# Revit family: okamura_81K2LH00-81K20KH_Zart_Swivel models With arm
name_source: partatom
category: 家具
revit_build: Autodesk Revit 2017 (Build: 20160225_1515(x64)
units: mm (PartAtom-declared; Revit-internal decimal feet)

## family parameters
OmniClass タイトル = General Furniture and Specialties
OmniClass 番号 = 23.40.20.00
ロード時にボイドで切り取り = いいえ
作業面に基づく = いいえ
共有 = いいえ
常に垂直 = はい
部屋計算ポイント = いいえ

## types (13) — shared parameters
Casters = okm_G155
D = 531  [stored 1.74213 ft]
Gas lift = okm_silver FX4
H = 854  [stored 2.80184 ft]
Kind = Chair
Leg = okm_silver FX4
Other = okm_G155
Product Categories = Seating
Product Name = Zart
URL = http://www.okamura.co.jp
W = 585  [stored 1.91929 ft]
アセンブリ コード = E2020200
キーノート = 12490
製造元 = Okamura Corporation

## per-type parameters (varying)
| type | Arm | Back & Seat | Common Specification | Product Number | Shell |
| 81W/FZF6（White/Sage） | okm_G272 | okm_FZF6 | White Shell | 81K2LH | okm_white 81W |
| 81W/FZF3（White/Lime Green） | okm_G272 | okm_FZF3 | White Shell | 81K2LH | okm_white 81W |
| 81W/FZF7（White/Yellow） | okm_G272 | okm_FZF7 | White Shell | 81K2LH | okm_white 81W |
| 81W/FZF8（White/Light Blue） | okm_G272 | okm_FZF8 | White Shell | 81K2LH | okm_white 81W |
| 81W/FZF9（White/White） | okm_G272 | okm_FZF9 | White Shell | 81K2LH | okm_white 81W |
| 81B/FZF1（Black/Black） | okm_G721 | okm_FZF1 | Black Shell | 81K2KH | okm_81B |
| 81B/FZF2（Black/Medium Blue） | okm_G721 | okm_FZF2 | Black Shell | 81K2KH | okm_81B |
| 81B/FZF3（Black/Lime Green） | okm_G721 | okm_FZF3 | Black Shell | 81K2KH | okm_81B |
| 81B/FZF4（Black/Red） | okm_G721 | okm_FZF4 | Black Shell | 81K2KH | okm_81B |
| 81B/FZF5（Black/Medium Gray） | okm_G721 | okm_FZF5 | Black Shell | 81K2KH | okm_81B |
| 81B/FZF6（Black/Sage） | okm_G721 | okm_FZF6 | Black Shell | 81K2KH | okm_81B |
| 81B/FZF7（Black/Yellow） | okm_G721 | okm_FZF7 | Black Shell | 81K2KH | okm_81B |
| 81B/FZF8（Black/Light Blue） | okm_G721 | okm_FZF8 | Black Shell | 81K2KH | okm_81B |

note: [stored X ft] marks values corroborated as IEEE doubles in the binary element streams (Revit-internal decimal feet)
